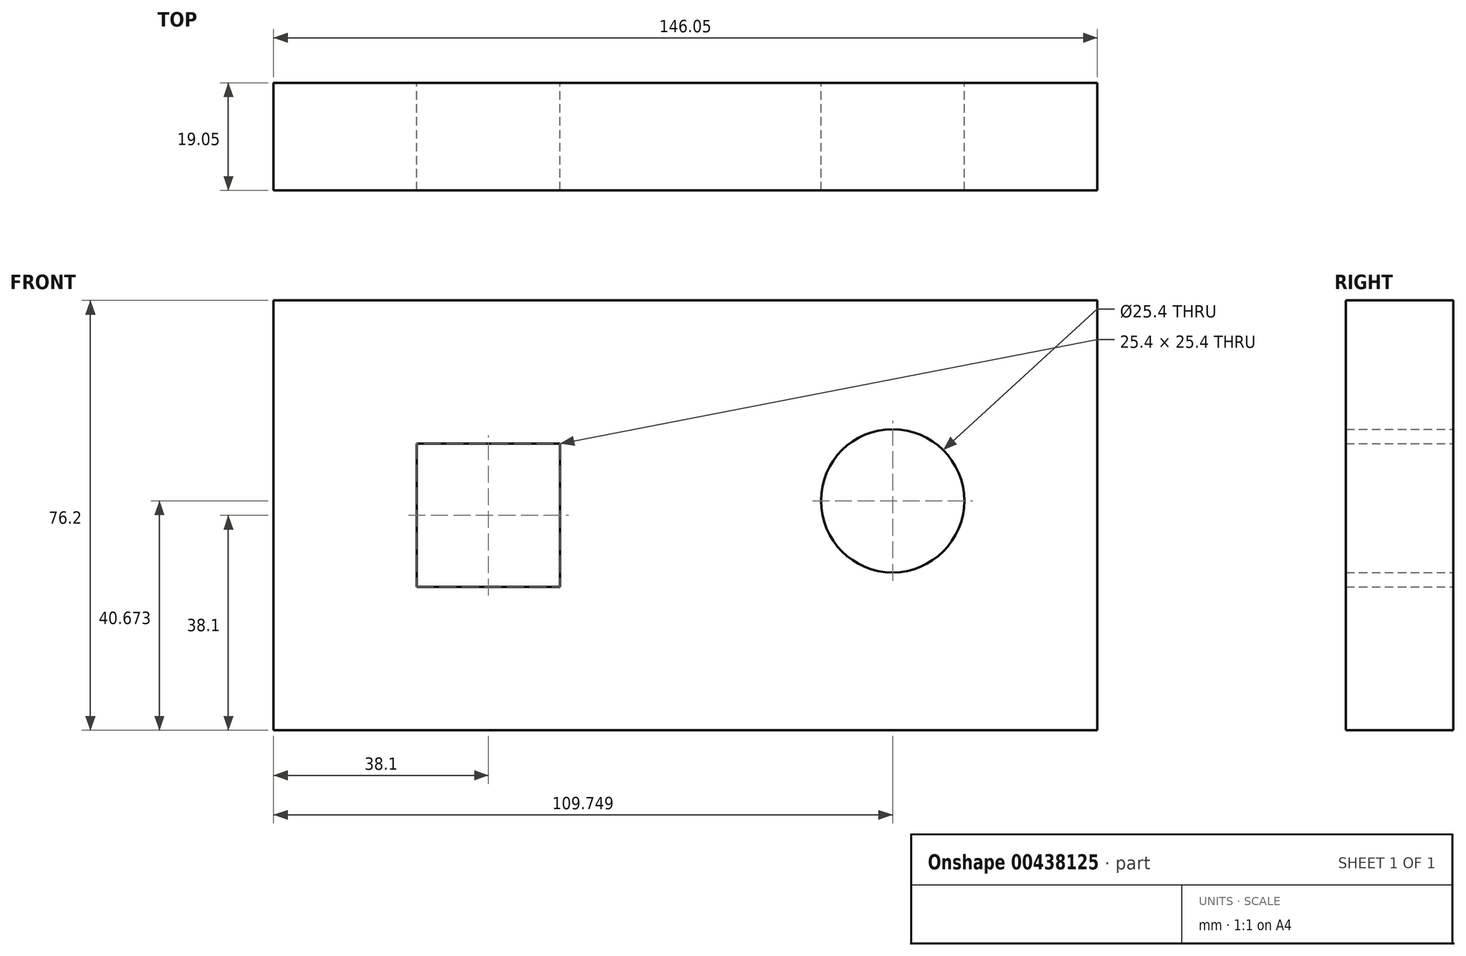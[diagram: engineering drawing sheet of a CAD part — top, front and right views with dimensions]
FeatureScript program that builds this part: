
annotation { "Feature Type Name" : "Feature", "Feature Type Description" : "" }
export const myFeature = defineFeature(function(context is Context, id is Id, definition is map)
    precondition{}
    {
        {
            var Q0;
            Q0=qCreatedBy(makeId("Front.planeOp"),FACE);
            var sketch = newSketch(context, id + "F0", { "sketchPlane" : qUnion([Q0])});
            skLineSegment(sketch, "E0.bottom", {"start": v(0, 0) * mm, "end": v(-146.05, 0) * mm});
            skLineSegment(sketch, "E0.top", {"start": v(0, 76.2) * mm, "end": v(-146.05, 76.2) * mm});
            skLineSegment(sketch, "E0.left", {"start": v(0, 0) * mm, "end": v(0, 76.2) * mm});
            skLineSegment(sketch, "E0.right", {"start": v(-146.05, 0) * mm, "end": v(-146.05, 76.2) * mm});
            skCircle(sketch, "E1", {"center": v(-36.3, 40.67) * mm, "radius": 12.7 * mm});
            skLineSegment(sketch, "E2.bottom", {"start": v(-95.25, 25.4) * mm, "end": v(-120.65, 25.4) * mm});
            skLineSegment(sketch, "E2.top", {"start": v(-95.25, 50.8) * mm, "end": v(-120.65, 50.8) * mm});
            skLineSegment(sketch, "E2.left", {"start": v(-95.25, 25.4) * mm, "end": v(-95.25, 50.8) * mm});
            skLineSegment(sketch, "E2.right", {"start": v(-120.65, 25.4) * mm, "end": v(-120.65, 50.8) * mm});
            skSolve(sketch);
        }
        {
            var Q0;
            Q0=makeQuery(id+"F0.imprint","IMPRINT",FACE,{"disambiguationData":[TD([[makeQuery(id+"F0.imprint","IMPRINT",EDGE,{"derivedFrom":sQuery(id+"F0.wireOp",EDGE,"E0.bottom")}),-1.0]])]});
            extrude(context, id + "F1", {"entities" : qUnion([Q0]), "depth" : 19.05 * mm});
        }
    });
